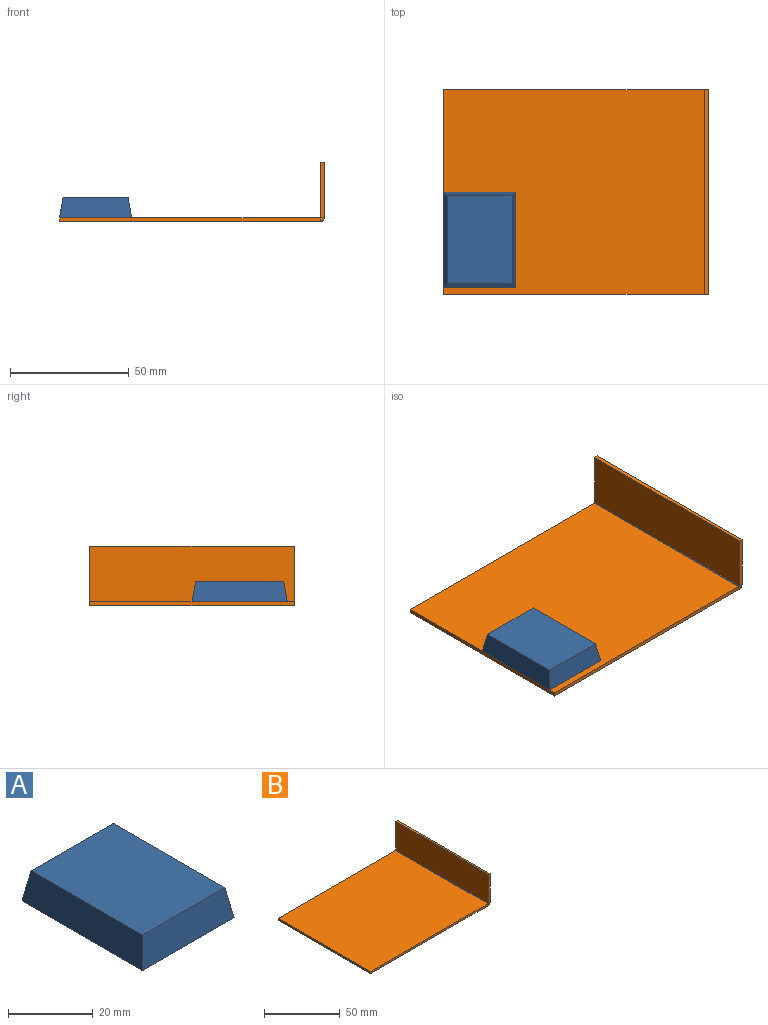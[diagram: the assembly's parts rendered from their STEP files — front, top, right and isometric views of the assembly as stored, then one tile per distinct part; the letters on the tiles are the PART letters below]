
ASSEMBLY  parts=2 mates=1
PART A: 6 faces, bbox 30.4x40.2x8.7 mm
  f0: plane 30.42x8.7mm, normal (0,-0.98,0.17), area 255.2mm2, adj f1,f3,f4,f5
  f1: plane 40.17x8.7mm, normal (0.98,0,0.17), area 341.3mm2, adj f0,f2,f4,f5
  f2: plane 30.42x8.7mm, normal (0,0.98,0.17), area 255.2mm2, adj f1,f3,f4,f5
  f3: plane 40.17x8.7mm, normal (-0.98,0,0.17), area 341.3mm2, adj f0,f2,f4,f5
  f4: plane 37.1x27.35mm, normal (0,0,1), area 1014.6mm2, adj f0,f1,f2,f3
  f5: plane 40.17x30.42mm, normal (0,0,-1), area 1221.8mm2, adj f0,f1,f2,f3
PART B: 14 faces, bbox 111.6x86.2x25 mm
  f0: plane 86.2x1.6mm, normal (-1,0,0), area 137.9mm2, adj f1,f2,f3,f4
  f1: plane 109.84x1.6mm, normal (0,1,0), area 175.7mm2, adj f0,f3,f4,f11
  f2: plane 109.84x1.6mm, normal (0,-1,0), area 175.7mm2, adj f0,f3,f4,f10
  f3: plane 109.84x86.2mm, normal (0,0,-1), area 9467.9mm2, adj f0,f1,f2,f12
  f4: plane 109.84x86.2mm, normal (0,0,1), area 9467.9mm2, adj f0,f1,f2,f13
  f5: plane 86.2x1.6mm, normal (0,0,1), area 137.9mm2, adj f6,f7,f8,f9
  f6: plane 23.2x1.6mm, normal (0,-1,0), area 37.1mm2, adj f5,f8,f9,f10
  f7: plane 23.2x1.6mm, normal (0,1,0), area 37.1mm2, adj f5,f8,f9,f11
  f8: plane 86.2x23.2mm, normal (1,0,0), area 1999.9mm2, adj f5,f6,f7,f12
  f9: plane 86.2x23.2mm, normal (-1,0,0), area 1999.9mm2, adj f5,f6,f7,f13
  f10: plane 1.8x1.8mm, normal (0,-1,0), area 2.5mm2, adj f2,f6,f12,f13
  f11: plane 1.8x1.8mm, normal (0,1,0), area 2.5mm2, adj f1,f7,f12,f13
  f12: cylinder r=1.8mm len=86.2mm, axis (0,-1,0), area 243.7mm2, adj f3,f8,f10,f11
  f13: cylinder r=0.2mm len=86.2mm, axis (0,-1,0), area 27.1mm2, adj f4,f9,f10,f11
PLACE A t=(-91.1,-30.83,-8.36)mm
PLACE B t=(-51.29,-10.75,-8.36)mm fixed
MATE fastened A.f5 <-> B.f4  axis (0,0,1) through (-106.31,-10.75,-6.76)mm
